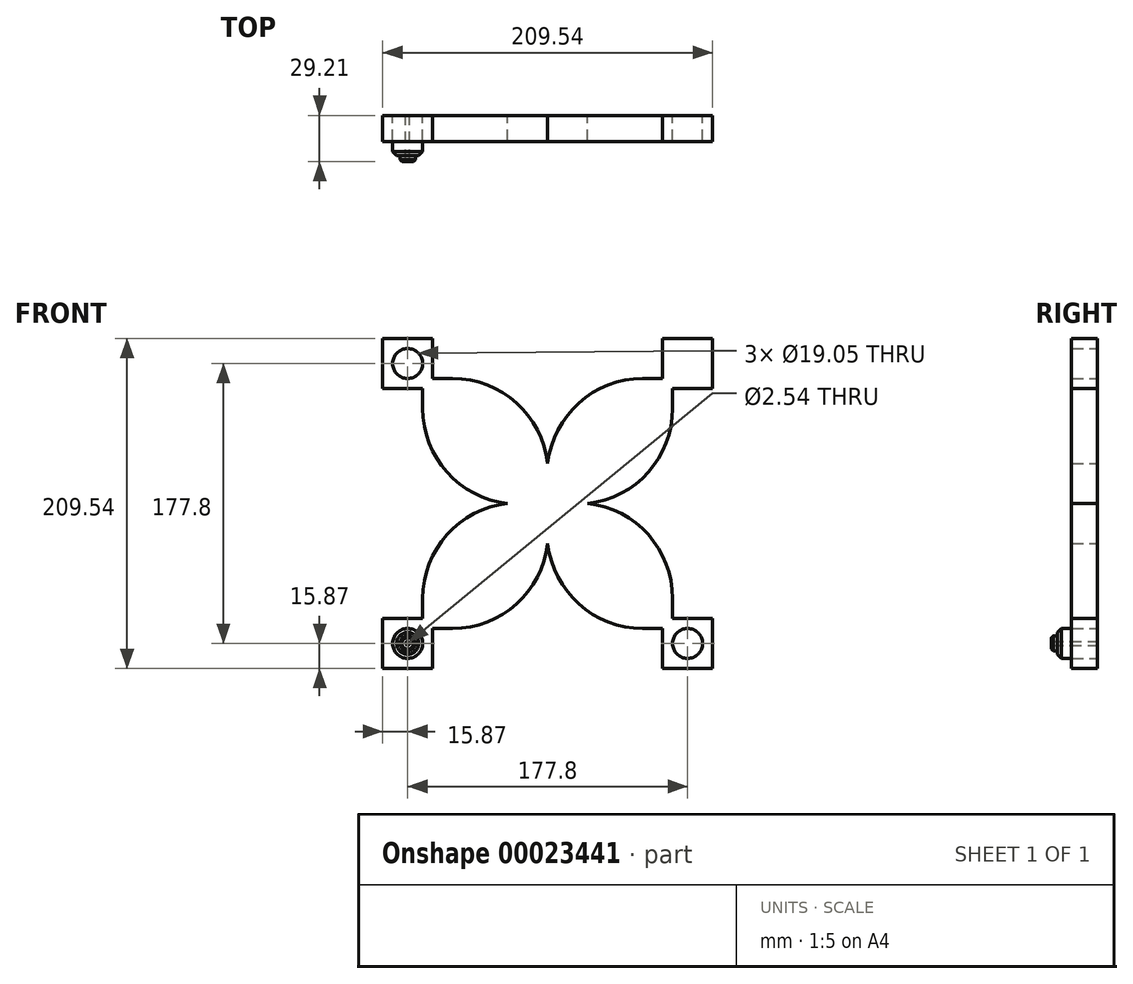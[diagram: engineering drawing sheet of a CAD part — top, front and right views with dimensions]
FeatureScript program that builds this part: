
annotation { "Feature Type Name" : "Feature", "Feature Type Description" : "" }
export const myFeature = defineFeature(function(context is Context, id is Id, definition is map)
    precondition{}
    {
        {
            var Q0;
            Q0=qCreatedBy(makeId("Front.planeOp"),FACE);
            var sketch = newSketch(context, id + "F0", { "sketchPlane" : qUnion([Q0])});
            skLineSegment(sketch, "E0.rect.bottom", {"start": v(88.9, -88.9) * mm, "end": v(-88.9, -88.9) * mm});
            skLineSegment(sketch, "E0.rect.top", {"start": v(88.9, 88.9) * mm, "end": v(-88.9, 88.9) * mm});
            skLineSegment(sketch, "E0.rect.left", {"start": v(88.9, -88.9) * mm, "end": v(88.9, 88.9) * mm});
            skLineSegment(sketch, "E0.rect.right", {"start": v(-88.9, -88.9) * mm, "end": v(-88.9, 88.9) * mm});
            skPoint(sketch, "E0.rect.middle", {"position": v(0, 0) * mm});
            skLineSegment(sketch, "E1", {"start": v(0, -88.9) * mm, "end": v(0, 88.9) * mm, "construction": true});
            skLineSegment(sketch, "E2", {"start": v(0, 0) * mm, "end": v(-88.9, 0) * mm, "construction": true});
            skLineSegment(sketch, "E3", {"start": v(0, 0) * mm, "end": v(-88.9, 88.9) * mm, "construction": true});
            skLineSegment(sketch, "E4", {"start": v(-88.9, 88.9) * mm, "end": v(-104.78, 104.78) * mm, "construction": true});
            skLineSegment(sketch, "E5.bottom", {"start": v(-73.03, 73.02) * mm, "end": v(-104.78, 73.02) * mm});
            skLineSegment(sketch, "E5.top", {"start": v(-73.03, 104.77) * mm, "end": v(-104.78, 104.77) * mm});
            skLineSegment(sketch, "E5.left", {"start": v(-73.03, 73.03) * mm, "end": v(-73.03, 104.78) * mm});
            skLineSegment(sketch, "E5.right", {"start": v(-104.78, 73.03) * mm, "end": v(-104.78, 104.78) * mm});
            skLineSegment(sketch, "E6.MirrorCS", {"start": v(73.03, 73.03) * mm, "end": v(73.03, 104.78) * mm});
            skLineSegment(sketch, "E7.MirrorCS", {"start": v(73.03, 73.02) * mm, "end": v(104.78, 73.02) * mm});
            skLineSegment(sketch, "E8.MirrorCS", {"start": v(104.78, 73.03) * mm, "end": v(104.78, 104.78) * mm});
            skLineSegment(sketch, "E9.MirrorCS", {"start": v(73.03, 104.77) * mm, "end": v(104.78, 104.77) * mm});
            skLineSegment(sketch, "E10.MirrorCS", {"start": v(73.03, -73.03) * mm, "end": v(104.78, -73.03) * mm});
            skLineSegment(sketch, "E11.MirrorCS", {"start": v(104.78, -73.03) * mm, "end": v(104.78, -104.78) * mm});
            skLineSegment(sketch, "E12.MirrorCS", {"start": v(73.03, -104.78) * mm, "end": v(104.78, -104.78) * mm});
            skLineSegment(sketch, "E13.MirrorCS", {"start": v(73.03, -73.03) * mm, "end": v(73.03, -104.78) * mm});
            skLineSegment(sketch, "E14.MirrorCS", {"start": v(-73.03, -73.03) * mm, "end": v(-73.03, -104.78) * mm});
            skLineSegment(sketch, "E15.MirrorCS", {"start": v(-73.03, -104.78) * mm, "end": v(-104.78, -104.78) * mm});
            skLineSegment(sketch, "E16.MirrorCS", {"start": v(-104.78, -73.03) * mm, "end": v(-104.78, -104.78) * mm});
            skLineSegment(sketch, "E17.MirrorCS", {"start": v(-73.03, -73.03) * mm, "end": v(-104.78, -73.03) * mm});
            skPoint(sketch, "E18.start.orphan", {"position": v(-25.4, 0) * mm});
            skLineSegment(sketch, "E19", {"start": v(-79.38, 73.02) * mm, "end": v(-79.38, 60.32) * mm});
            skArc(sketch, "E20", {"start": v(-79.37, 60.32) * mm, "mid": v(-63.91, 19.85) * mm, "end": v(-25.4, 0) * mm});
            skArc(sketch, "E21.MirrorCS", {"start": v(-79.37, -60.32) * mm, "mid": v(-63.91, -19.85) * mm, "end": v(-25.4, 0) * mm});
            skLineSegment(sketch, "E22.MirrorCS", {"start": v(-79.38, -73.02) * mm, "end": v(-79.38, -60.32) * mm});
            skArc(sketch, "E23.1.0", {"start": v(-60.32, -79.37) * mm, "mid": v(-19.85, -63.91) * mm, "end": v(0, -25.4) * mm});
            skArc(sketch, "E23.1.1", {"start": v(60.32, -79.37) * mm, "mid": v(19.85, -63.91) * mm, "end": v(0, -25.4) * mm});
            skLineSegment(sketch, "E23.1.2", {"start": v(73.02, -79.38) * mm, "end": v(60.32, -79.38) * mm});
            skLineSegment(sketch, "E23.1.3", {"start": v(-73.02, -79.38) * mm, "end": v(-60.32, -79.38) * mm});
            skArc(sketch, "E23.2.0", {"start": v(79.37, -60.32) * mm, "mid": v(63.91, -19.85) * mm, "end": v(25.4, 0) * mm});
            skArc(sketch, "E23.2.1", {"start": v(79.37, 60.32) * mm, "mid": v(63.91, 19.85) * mm, "end": v(25.4, 0) * mm});
            skLineSegment(sketch, "E23.2.2", {"start": v(79.38, 73.02) * mm, "end": v(79.38, 60.32) * mm});
            skLineSegment(sketch, "E23.2.3", {"start": v(79.37, -73.03) * mm, "end": v(79.37, -60.33) * mm});
            skArc(sketch, "E23.3.0", {"start": v(60.32, 79.37) * mm, "mid": v(19.85, 63.91) * mm, "end": v(0, 25.4) * mm});
            skArc(sketch, "E23.3.1", {"start": v(-60.32, 79.38) * mm, "mid": v(-19.85, 63.91) * mm, "end": v(0, 25.4) * mm});
            skLineSegment(sketch, "E23.3.2", {"start": v(-73.02, 79.38) * mm, "end": v(-60.32, 79.38) * mm});
            skLineSegment(sketch, "E23.3.3", {"start": v(73.03, 79.37) * mm, "end": v(60.33, 79.37) * mm});
            skSolve(sketch);
        }
        {
            var Q0;
            {var subQ15=sQuery(id+"F0.wireOp",EDGE,"E19");Q0=makeQuery(id+"F0.imprint","IMPRINT",FACE,{"disambiguationData":[TD([[makeQuery(id+"F0.imprint","IMPRINT",EDGE,{"derivedFrom":subQ15}),1.0]])]});}
            var Q1;
            {var subQ1=sQuery(id+"F0.wireOp",EDGE,"E5.top");Q1=makeQuery(id+"F0.imprint","IMPRINT",FACE,{"disambiguationData":[TD([[makeQuery(id+"F0.imprint","IMPRINT",EDGE,{"derivedFrom":subQ1}),1.0]])]});}
            var Q2;
            {var subQ1=sQuery(id+"F0.wireOp",EDGE,"E0.rect.top");var subQ6=sQuery(id+"F0.wireOp",EDGE,"E0.rect.right");var subQ9=makeQuery(id+"F0.imprint","INTERSECT",VERTEX,{"derivedFrom":[subQ1,subQ6]});Q2=makeQuery(id+"F0.imprint","IMPRINT",FACE,{"disambiguationData":[TD([[makeQuery(id+"F0.imprint","IMPRINT",EDGE,{"disambiguationData":[TD([[subQ9,1.0]])],"derivedFrom":subQ1}),1.0]])]});}
            var Q3;
            {var subQ1=sQuery(id+"F0.wireOp",EDGE,"E0.rect.right");var subQ6=sQuery(id+"F0.wireOp",EDGE,"E0.rect.bottom");var subQ9=makeQuery(id+"F0.imprint","INTERSECT",VERTEX,{"derivedFrom":[subQ6,subQ1]});Q3=makeQuery(id+"F0.imprint","IMPRINT",FACE,{"disambiguationData":[TD([[makeQuery(id+"F0.imprint","IMPRINT",EDGE,{"disambiguationData":[TD([[subQ9,1.0]])],"derivedFrom":subQ6}),-1.0]])]});}
            var Q4;
            {var subQ4=sQuery(id+"F0.wireOp",EDGE,"E15.MirrorCS");Q4=makeQuery(id+"F0.imprint","IMPRINT",FACE,{"disambiguationData":[TD([[makeQuery(id+"F0.imprint","IMPRINT",EDGE,{"derivedFrom":subQ4}),-1.0]])]});}
            var Q5;
            {var subQ4=sQuery(id+"F0.wireOp",EDGE,"E11.MirrorCS");Q5=makeQuery(id+"F0.imprint","IMPRINT",FACE,{"disambiguationData":[TD([[makeQuery(id+"F0.imprint","IMPRINT",EDGE,{"derivedFrom":subQ4}),-1.0]])]});}
            var Q6;
            {var subQ1=sQuery(id+"F0.wireOp",EDGE,"E0.rect.bottom");var subQ6=sQuery(id+"F0.wireOp",EDGE,"E0.rect.left");var subQ9=makeQuery(id+"F0.imprint","INTERSECT",VERTEX,{"derivedFrom":[subQ1,subQ6]});Q6=makeQuery(id+"F0.imprint","IMPRINT",FACE,{"disambiguationData":[TD([[makeQuery(id+"F0.imprint","IMPRINT",EDGE,{"disambiguationData":[TD([[subQ9,-1.0]])],"derivedFrom":subQ1}),-1.0]])]});}
            var Q7;
            {var subQ1=sQuery(id+"F0.wireOp",EDGE,"E0.rect.left");var subQ6=sQuery(id+"F0.wireOp",EDGE,"E0.rect.top");var subQ7=makeQuery(id+"F0.imprint","INTERSECT",VERTEX,{"derivedFrom":[subQ6,subQ1]});Q7=makeQuery(id+"F0.imprint","IMPRINT",FACE,{"disambiguationData":[TD([[makeQuery(id+"F0.imprint","IMPRINT",EDGE,{"disambiguationData":[TD([[subQ7,-1.0]])],"derivedFrom":subQ6}),1.0]])]});}
            var Q8;
            {var subQ1=sQuery(id+"F0.wireOp",EDGE,"E8.MirrorCS");Q8=makeQuery(id+"F0.imprint","IMPRINT",FACE,{"disambiguationData":[TD([[makeQuery(id+"F0.imprint","IMPRINT",EDGE,{"derivedFrom":subQ1}),1.0]])]});}
            extrude(context, id + "F1", {"entities" : qUnion([Q0, Q1, Q2, Q3, Q4, Q5, Q6, Q7, Q8]), "depth" : 16.5 * mm});
        }
        {
            var Q0;
            Q0=sQuery(id+"F0.wireOp",VERTEX,"E0.rect.right.end");
            var Q1;
            Q1=sQuery(id+"F0.wireOp",VERTEX,"E0.rect.left.end");
            var Q2;
            Q2=sQuery(id+"F0.wireOp",VERTEX,"E0.rect.right.start");
            var Q3;
            Q3=sQuery(id+"F0.wireOp",VERTEX,"E0.rect.left.start");
            var Q4;
            Q4=makeQuery(id+"F1.opExtrude","SWEPT_BODY",BODY,{"disambiguationData":[OSD([sQuery(id+"F0.wireOp",EDGE,"E0.rect.bottom"),sQuery(id+"F0.wireOp",EDGE,"E0.rect.top"),sQuery(id+"F0.wireOp",EDGE,"E0.rect.right"),sQuery(id+"F0.wireOp",EDGE,"E5.bottom"),sQuery(id+"F0.wireOp",EDGE,"E5.top"),sQuery(id+"F0.wireOp",EDGE,"E5.left"),sQuery(id+"F0.wireOp",EDGE,"E5.right"),sQuery(id+"F0.wireOp",EDGE,"E6.MirrorCS"),sQuery(id+"F0.wireOp",EDGE,"E0.rect.left"),sQuery(id+"F0.wireOp",EDGE,"E7.MirrorCS"),sQuery(id+"F0.wireOp",EDGE,"E8.MirrorCS"),sQuery(id+"F0.wireOp",EDGE,"E9.MirrorCS"),sQuery(id+"F0.wireOp",EDGE,"E10.MirrorCS"),sQuery(id+"F0.wireOp",EDGE,"E11.MirrorCS"),sQuery(id+"F0.wireOp",EDGE,"E12.MirrorCS"),sQuery(id+"F0.wireOp",EDGE,"E13.MirrorCS"),sQuery(id+"F0.wireOp",EDGE,"E14.MirrorCS"),sQuery(id+"F0.wireOp",EDGE,"E15.MirrorCS"),sQuery(id+"F0.wireOp",EDGE,"E16.MirrorCS"),sQuery(id+"F0.wireOp",EDGE,"E17.MirrorCS")])]});
            hole(context, id + "F2", {"style" : HoleStyle.SIMPLE, "holeDiameter" : 19.05 * mm, "endStyle" : HoleEndStyle.THROUGH, "oppositeDirection" : true, "locations" : qUnion([Q0, Q1, Q2, Q3]), "scope" : qUnion([Q4])});
        }
        {
            var Q0;
            Q0=makeQuery(id+"F1.opExtrude","CAP_FACE",FACE,{"disambiguationData":[OSD([sQuery(id+"F0.wireOp",EDGE,"E0.rect.bottom"),sQuery(id+"F0.wireOp",EDGE,"E0.rect.top"),sQuery(id+"F0.wireOp",EDGE,"E0.rect.right"),sQuery(id+"F0.wireOp",EDGE,"E5.bottom"),sQuery(id+"F0.wireOp",EDGE,"E5.top"),sQuery(id+"F0.wireOp",EDGE,"E5.left"),sQuery(id+"F0.wireOp",EDGE,"E5.right"),sQuery(id+"F0.wireOp",EDGE,"E6.MirrorCS"),sQuery(id+"F0.wireOp",EDGE,"E0.rect.left"),sQuery(id+"F0.wireOp",EDGE,"E7.MirrorCS"),sQuery(id+"F0.wireOp",EDGE,"E8.MirrorCS"),sQuery(id+"F0.wireOp",EDGE,"E9.MirrorCS"),sQuery(id+"F0.wireOp",EDGE,"E10.MirrorCS"),sQuery(id+"F0.wireOp",EDGE,"E11.MirrorCS"),sQuery(id+"F0.wireOp",EDGE,"E12.MirrorCS"),sQuery(id+"F0.wireOp",EDGE,"E13.MirrorCS"),sQuery(id+"F0.wireOp",EDGE,"E14.MirrorCS"),sQuery(id+"F0.wireOp",EDGE,"E15.MirrorCS"),sQuery(id+"F0.wireOp",EDGE,"E16.MirrorCS"),sQuery(id+"F0.wireOp",EDGE,"E17.MirrorCS")])],"isStart":true});
            var sketch = newSketch(context, id + "F3", { "sketchPlane" : qUnion([Q0])});
            skCircle(sketch, "E24.0", {"center": v(88.9, -88.9) * mm, "radius": 9.53 * mm});
            skCircle(sketch, "E25", {"center": v(88.9, -88.9) * mm, "radius": 4.89 * mm});
            skCircle(sketch, "E26", {"center": v(88.9, -88.9) * mm, "radius": 1.27 * mm});
            skSolve(sketch);
        }
        {
            var Q0;
            Q0 = qSketchRegion(id + "F3", true);
            extrude(context, id + "F4", {"entities" : qUnion([Q0]), "oppositeDirection" : true, "depth" : 25.4 * mm});
        }
        {
            var Q0;
            Q0=makeQuery(id+"F3.imprint","IMPRINT",FACE,{"disambiguationData":[TD([[makeQuery(id+"F3.imprint","IMPRINT",EDGE,{"derivedFrom":sQuery(id+"F3.wireOp",EDGE,"E25")}),1.0]])]});
            extrude(context, id + "F5", {"entities" : qUnion([Q0]), "operationType" : NewBodyOperationType.ADD, "oppositeDirection" : true, "depth" : 29.2 * mm});
        }
        {
            var Q0;
            Q0=makeQuery(id+"F4.opExtrude","CAP_EDGE",EDGE,{"disambiguationData":[OSD([sQuery(id+"F3.wireOp",EDGE,"E24.0")])],"isStart":false});
            chamfer(context, id + "F6", {"entities" : qUnion([Q0]), "width" : 2.54 * mm, "tangentPropagation" : true});
        }
        {
            var Q0;
            Q0=makeQuery(id+"F5.opExtrude","CAP_EDGE",EDGE,{"disambiguationData":[OSD([sQuery(id+"F3.wireOp",EDGE,"E25")])],"isStart":false});
            chamfer(context, id + "F7", {"entities" : qUnion([Q0]), "width" : 1.27 * mm, "tangentPropagation" : true});
        }
    });
